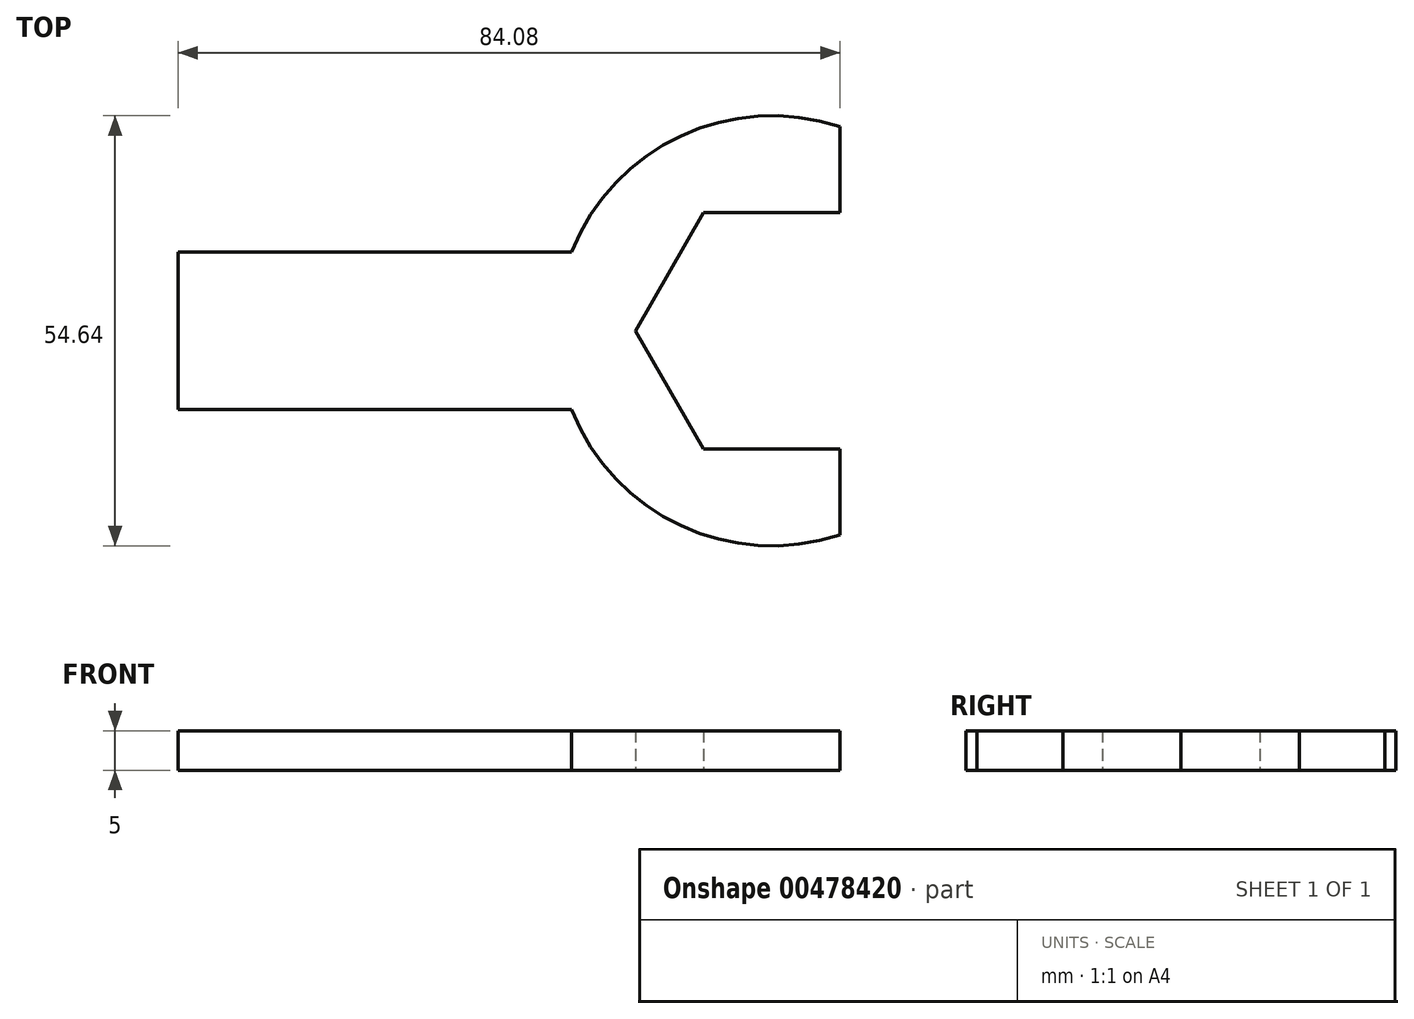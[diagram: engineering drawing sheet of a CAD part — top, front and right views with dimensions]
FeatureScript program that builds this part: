
annotation { "Feature Type Name" : "Feature", "Feature Type Description" : "" }
export const myFeature = defineFeature(function(context is Context, id is Id, definition is map)
    precondition{}
    {
        {
            var Q0;
            Q0=qCreatedBy(makeId("Top.planeOp"),FACE);
            var sketch = newSketch(context, id + "F0", { "sketchPlane" : qUnion([Q0])});
            skArc(sketch, "E0.cCircle", {"start": v(0, 15) * mm, "mid": v(-15, 0) * mm, "end": v(0, -15) * mm, "construction": true});
            skLineSegment(sketch, "E0.0", {"start": v(8.66, -15) * mm, "end": v(0, -15) * mm});
            skLineSegment(sketch, "E0.1", {"start": v(-8.66, -15) * mm, "end": v(-17.32, 0) * mm});
            skLineSegment(sketch, "E0.2", {"start": v(-17.32, 0) * mm, "end": v(-8.66, 15) * mm});
            skLineSegment(sketch, "E0.3", {"start": v(-8.66, 15) * mm, "end": v(0, 15) * mm});
            skPoint(sketch, "E0.0.midPoint", {"position": v(0, -15) * mm});
            skLineSegment(sketch, "E1", {"start": v(-25.42, 10) * mm, "end": v(-75.42, 10) * mm});
            skLineSegment(sketch, "E2", {"start": v(-75.42, 10) * mm, "end": v(-75.42, -10) * mm});
            skLineSegment(sketch, "E3", {"start": v(-75.42, -10) * mm, "end": v(-25.42, -10) * mm});
            skLineSegment(sketch, "E4", {"start": v(0, -110.88) * mm, "end": v(0, 116.47) * mm, "construction": true});
            skArc(sketch, "E5", {"start": v(0, 27.32) * mm, "mid": v(-15.38, 22.58) * mm, "end": v(-25.42, 10) * mm});
            skArc(sketch, "E6", {"start": v(0, -27.32) * mm, "mid": v(4.39, -26.97) * mm, "end": v(8.66, -25.91) * mm});
            skLineSegment(sketch, "E7", {"start": v(0, -15) * mm, "end": v(-8.66, -15) * mm});
            skLineSegment(sketch, "E8", {"start": v(0, 15) * mm, "end": v(8.66, 15) * mm});
            skLineSegment(sketch, "E9", {"start": v(8.66, 15) * mm, "end": v(8.66, 25.91) * mm});
            skLineSegment(sketch, "E10", {"start": v(8.66, -15) * mm, "end": v(8.66, -25.91) * mm});
            skArc(sketch, "E11.trimOffspring", {"start": v(8.66, 25.91) * mm, "mid": v(4.39, 26.97) * mm, "end": v(0, 27.32) * mm});
            skPoint(sketch, "E12.orphan", {"position": v(17.32, 0) * mm});
            skArc(sketch, "E13.trimOffspring", {"start": v(-25.42, -10) * mm, "mid": v(-15.38, -22.58) * mm, "end": v(0, -27.32) * mm});
            skSolve(sketch);
        }
        {
            var Q0;
            Q0=makeQuery(id+"F0.imprint","IMPRINT",FACE,{"disambiguationData":[TD([[makeQuery(id+"F0.imprint","IMPRINT",EDGE,{"derivedFrom":sQuery(id+"F0.wireOp",EDGE,"E0.0")}),1.0]])]});
            extrude(context, id + "F1", {"entities" : qUnion([Q0]), "depth" : 5 * mm});
        }
    });
